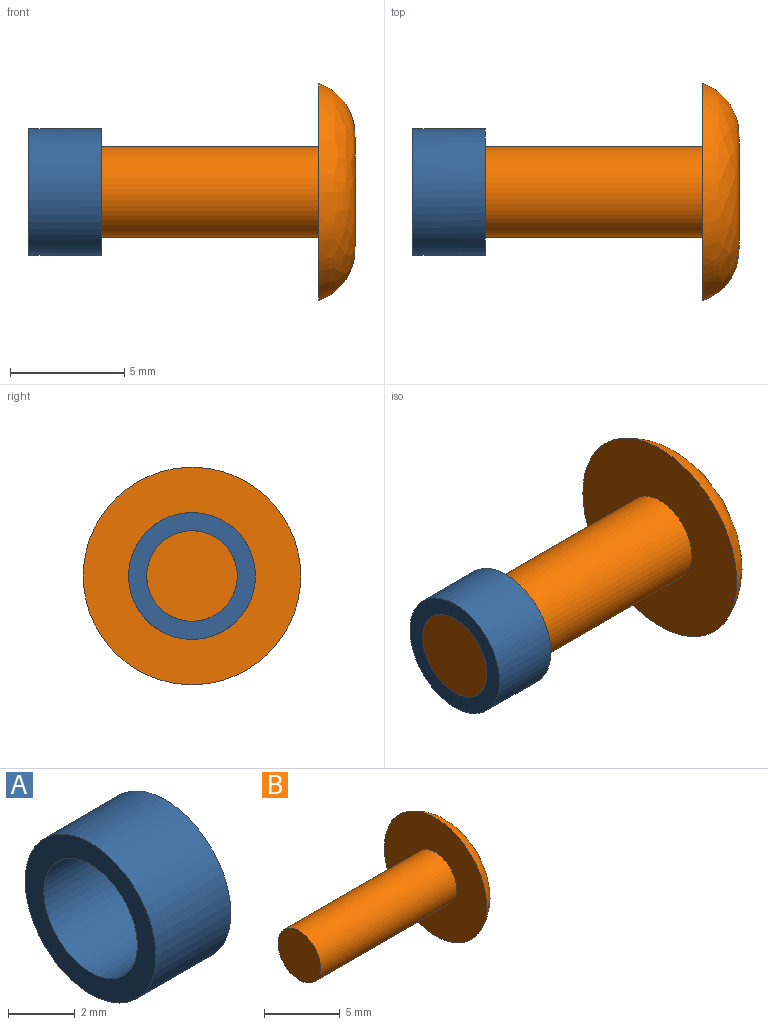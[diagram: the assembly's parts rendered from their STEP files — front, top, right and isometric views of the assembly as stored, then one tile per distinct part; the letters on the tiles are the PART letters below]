
ASSEMBLY  parts=2 mates=1
PART A: 4 faces, bbox 3.2x5.6x5.6 mm
  f0: plane 5.56x5.56mm, normal (-1,0,0), area 11.9mm2, adj f1,f2
  f1: cylinder r=1.98mm len=3.97mm, axis (1,0,0), area 39.6mm2, adj f0,f3
  f2: cylinder r=2.78mm len=5.56mm, axis (1,0,0), area 55.4mm2, adj f0,f3
  f3: plane 5.56x5.56mm, normal (1,0,0), area 11.9mm2, adj f1,f2
PART B: 5 faces, bbox 14.3x9.5x9.5 mm
  f0: plane 4.82x4.82mm, normal (1,0,0), area 18.2mm2, adj f2
  f1: plane 9.54x9.54mm, normal (-1,0,0), area 58.9mm2, adj f2,f3
  f2: bspline ~9.53x9.53mm, area 71.8mm2, adj f0,f1
  f3: cylinder r=1.98mm len=12.7mm, axis (1,0,0), area 158.3mm2, adj f1,f4
  f4: plane 3.97x3.97mm, normal (-1,0,0), area 12.4mm2, adj f3
PLACE A t=(-3.17,38.1,0)mm
PLACE B at identity fixed
MATE fastened A.f1 <-> B.f3  axis (1,0,0) through (28.57,-11.62,14.41)mm
